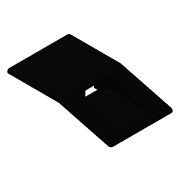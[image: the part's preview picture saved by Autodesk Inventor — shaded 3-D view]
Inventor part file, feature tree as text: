
AUTODESK INVENTOR PART (.ipt)
format: ipt  version: 2013 (Build 170138000, 138)  size: 217,088 bytes
history: native  units: in
note: dims shown in document units (in); Inventor stores cm internally (conversion verified against a paired STEP export)
features: sketch x8, extrude x6, fillet x5, hole x2, plane x1
ambient origin geometry x8: Origin, YZ Plane, XZ Plane, XY Plane, X Axis, Y Axis, Z Axis, Center Point
bodies: Solid1 (feature_tree)
feature tree (22):
  extrude  "Extrusion1"  Depth=0.1in
  fillet  "Fillet6"  Radius=1.8in
  extrude  "Extrusion10"  Depth=0.375in
  extrude  "Extrusion11"  Depth=1.025in
  extrude  "Extrusion12"  Depth=0.4in
  extrude  "Extrusion13"  Depth=0.1in
  extrude  "Extrusion15"  Depth=1.4in TaperAngle=0.0deg
  fillet  "Fillet7"  Radius=1.5375in
  fillet  "Fillet8"  Radius=0.45in
  fillet  "Fillet9"  Radius=0.25in
  fillet  "Fillet10"  Radius=0.175in
  plane  "Work Plane2"
  sketch  "Sketch16"  dims[d60=1.5375in d61=0.0in d62=0.0in]
  hole  "Hole1"  [1 undecoded]
  hole  "Hole2"  [1 undecoded]
  sketch  "Sketch1"  dims[d3=1.5in d4=0.1in d6=1.8in d7=0.0in]
  sketch  "Sketch9"  dims[d24=0.0625in d35=0.375in]
  sketch  "Sketch10"  dims[d42=0.063in d43=1.025in]
  sketch  "Sketch11"  dims[d44=0.3875in d45=0.4in]
  sketch  "Sketch12"  dims[d46=1.5in d47=0.0in d48=0.1in]
  sketch  "Sketch13"  dims[d49=0.1in d51=1.4in d52=0.0in d53=1.5375in d54=0.0in d55=0.45in d56=0.25in d57=0.175in]
  sketch  "Sketch18"  dims[d64=1.5in d67=0.4in d68=0.063in d69=0.1in d70=0.0in d71=0.0625in d72=0.0625in d73=0.0625in d74=0.0625in d82=0.0in d83=0.0625in d84=0.1in d85=0.1in d86=0.0625in d87=0.1in d99=0.063in d100=0.75in d101=0.1181in d102=0.05in d103=0.5635in d104=1.0in d105=0.8108in d106=0.063in d107=0.75in d108=0.1181in d109=0.075in d110=0.5635in d111=1.0in d112=0.8108in]
note: 2 required parameter values undecoded (feature->parameter linkage not recoverable at this tier; creation-order binding heuristic only, values carry confidence <= 0.55)
